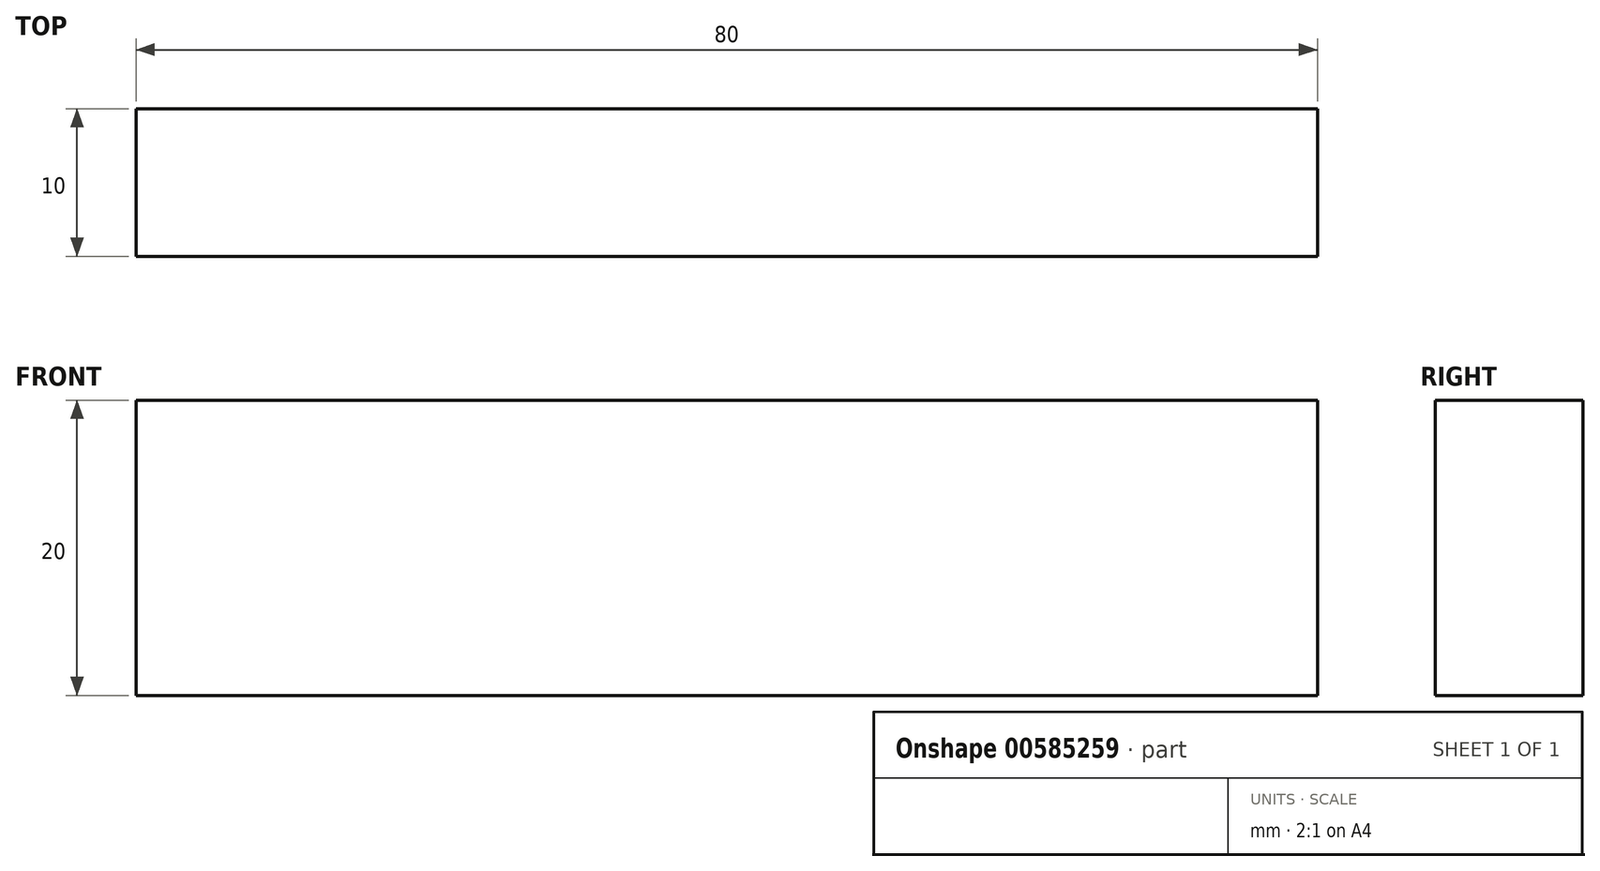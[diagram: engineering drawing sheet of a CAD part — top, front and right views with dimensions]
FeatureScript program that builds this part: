
annotation { "Feature Type Name" : "Feature", "Feature Type Description" : "" }
export const myFeature = defineFeature(function(context is Context, id is Id, definition is map)
    precondition{}
    {
        {
            var Q0;
            Q0=qCreatedBy(makeId("Front.planeOp"),FACE);
            var sketch = newSketch(context, id + "F0", { "sketchPlane" : qUnion([Q0])});
            skLineSegment(sketch, "E0.bottom", {"start": v(-74.67, -13.39) * mm, "end": v(5.33, -13.39) * mm});
            skLineSegment(sketch, "E0.top", {"start": v(-74.67, -33.39) * mm, "end": v(5.33, -33.39) * mm});
            skLineSegment(sketch, "E0.left", {"start": v(-74.67, -13.39) * mm, "end": v(-74.67, -33.39) * mm});
            skLineSegment(sketch, "E0.right", {"start": v(5.33, -13.39) * mm, "end": v(5.33, -33.39) * mm});
            skSolve(sketch);
        }
        {
            var Q0;
            Q0 = qSketchRegion(id + "F0", true);
            extrude(context, id + "F1", {"entities" : qUnion([Q0]), "depth" : 10 * mm, "offsetDistance" : 25 * mm});
        }
    });
